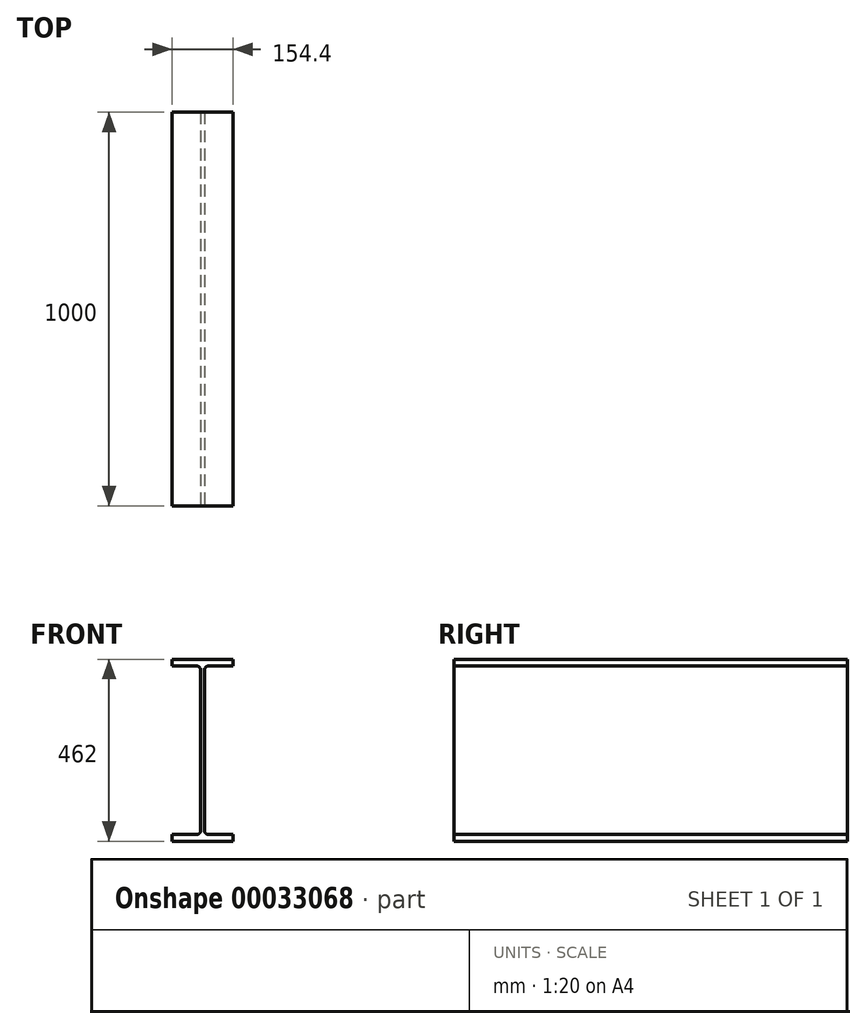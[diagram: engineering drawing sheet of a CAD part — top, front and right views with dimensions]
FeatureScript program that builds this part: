
annotation { "Feature Type Name" : "Feature", "Feature Type Description" : "" }
export const myFeature = defineFeature(function(context is Context, id is Id, definition is map)
    precondition{}
    {
        {
            var Q0;
            Q0=qCreatedBy(makeId("Front.planeOp"),FACE);
            var sketch = newSketch(context, id + "F0", { "sketchPlane" : qUnion([Q0])});
            skLineSegment(sketch, "E0", {"start": v(-72.4, 541.24) * mm, "end": v(82, 541.24) * mm});
            skLineSegment(sketch, "E1", {"start": v(82, 541.24) * mm, "end": v(82, 558.24) * mm});
            skLineSegment(sketch, "E2", {"start": v(82, 558.24) * mm, "end": v(19.8, 558.24) * mm});
            skLineSegment(sketch, "E3", {"start": v(9.6, 568.44) * mm, "end": v(9.6, 976.04) * mm});
            skLineSegment(sketch, "E4", {"start": v(19.8, 986.24) * mm, "end": v(82, 986.24) * mm});
            skLineSegment(sketch, "E5", {"start": v(82, 986.24) * mm, "end": v(82, 1003.24) * mm});
            skLineSegment(sketch, "E6", {"start": v(82, 1003.24) * mm, "end": v(-72.4, 1003.24) * mm});
            skLineSegment(sketch, "E7", {"start": v(-72.4, 1003.24) * mm, "end": v(-72.4, 986.24) * mm});
            skLineSegment(sketch, "E8", {"start": v(-72.4, 986.24) * mm, "end": v(-10.2, 986.24) * mm});
            skLineSegment(sketch, "E9", {"start": v(0, 976.04) * mm, "end": v(0, 568.44) * mm});
            skLineSegment(sketch, "E10", {"start": v(-10.2, 558.24) * mm, "end": v(-72.4, 558.24) * mm});
            skLineSegment(sketch, "E11", {"start": v(-72.4, 558.24) * mm, "end": v(-72.4, 541.24) * mm});
            skPoint(sketch, "E12.visualSharp", {"position": v(9.6, 558.24) * mm});
            skArc(sketch, "E12.filletArc", {"start": v(9.6, 568.44) * mm, "mid": v(12.59, 561.23) * mm, "end": v(19.8, 558.24) * mm});
            skPoint(sketch, "E13.visualSharp", {"position": v(0, 558.24) * mm});
            skArc(sketch, "E13.filletArc", {"start": v(-10.2, 558.24) * mm, "mid": v(-2.99, 561.23) * mm, "end": v(0, 568.44) * mm});
            skPoint(sketch, "E14.visualSharp", {"position": v(9.6, 986.24) * mm});
            skArc(sketch, "E14.filletArc", {"start": v(19.8, 986.24) * mm, "mid": v(12.59, 983.25) * mm, "end": v(9.6, 976.04) * mm});
            skPoint(sketch, "E15.visualSharp", {"position": v(0, 986.24) * mm});
            skArc(sketch, "E15.filletArc", {"start": v(0, 976.04) * mm, "mid": v(-2.99, 983.25) * mm, "end": v(-10.2, 986.24) * mm});
            skSolve(sketch);
        }
        {
            var Q0;
            Q0 = qSketchRegion(id + "F0", true);
            extrude(context, id + "F1", {"entities" : qUnion([Q0]), "oppositeDirection" : true, "depth" : 1000 * mm});
        }
    });
